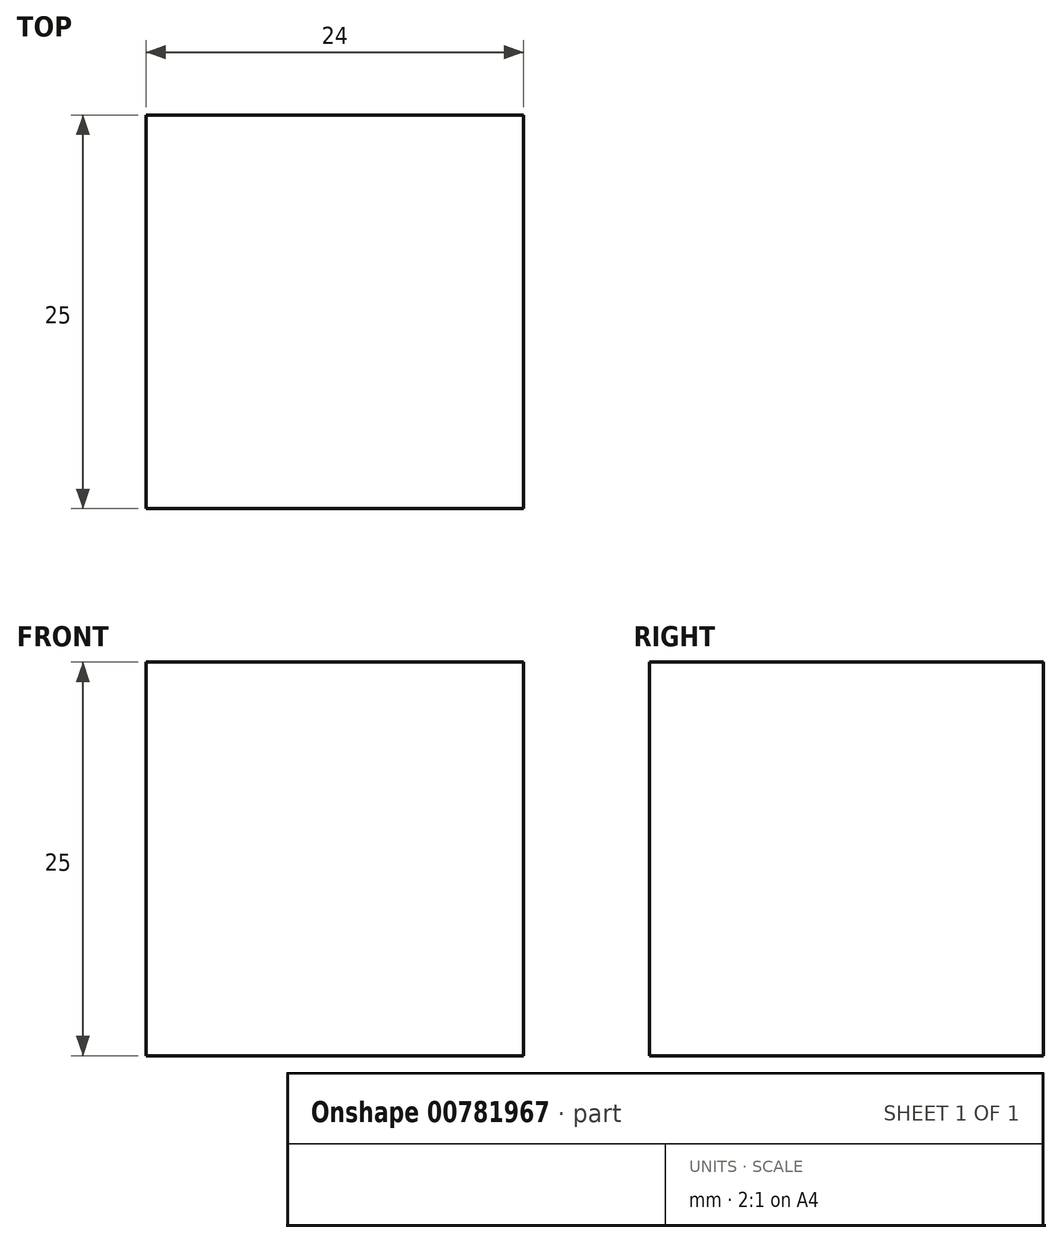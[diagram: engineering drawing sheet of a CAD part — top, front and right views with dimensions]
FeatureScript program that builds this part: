
annotation { "Feature Type Name" : "Feature", "Feature Type Description" : "" }
export const myFeature = defineFeature(function(context is Context, id is Id, definition is map)
    precondition{}
    {
        {
            var Q0;
            Q0=qCreatedBy(makeId("Front.planeOp"),FACE);
            var sketch = newSketch(context, id + "F0", { "sketchPlane" : qUnion([Q0])});
            skLineSegment(sketch, "E0.bottom", {"start": v(11.71, 12.54) * mm, "end": v(-13.29, 12.54) * mm});
            skLineSegment(sketch, "E0.top", {"start": v(11.71, -12.46) * mm, "end": v(-388.29, -12.46) * mm});
            skLineSegment(sketch, "E0.left", {"start": v(11.71, 12.54) * mm, "end": v(11.71, -12.46) * mm});
            skLineSegment(sketch, "E0.right", {"start": v(-12.29, 12.54) * mm, "end": v(-12.29, -12.46) * mm});
            skSolve(sketch);
        }
        {
            var Q0;
            Q0=qSketchRegion(id+"F0",true);
            extrude(context, id + "F1", {"entities" : qUnion([Q0]), "endBound" : BoundingType.SYMMETRIC, "depth" : 25 * mm, "offsetDistance" : 25 * mm});
        }
    });
